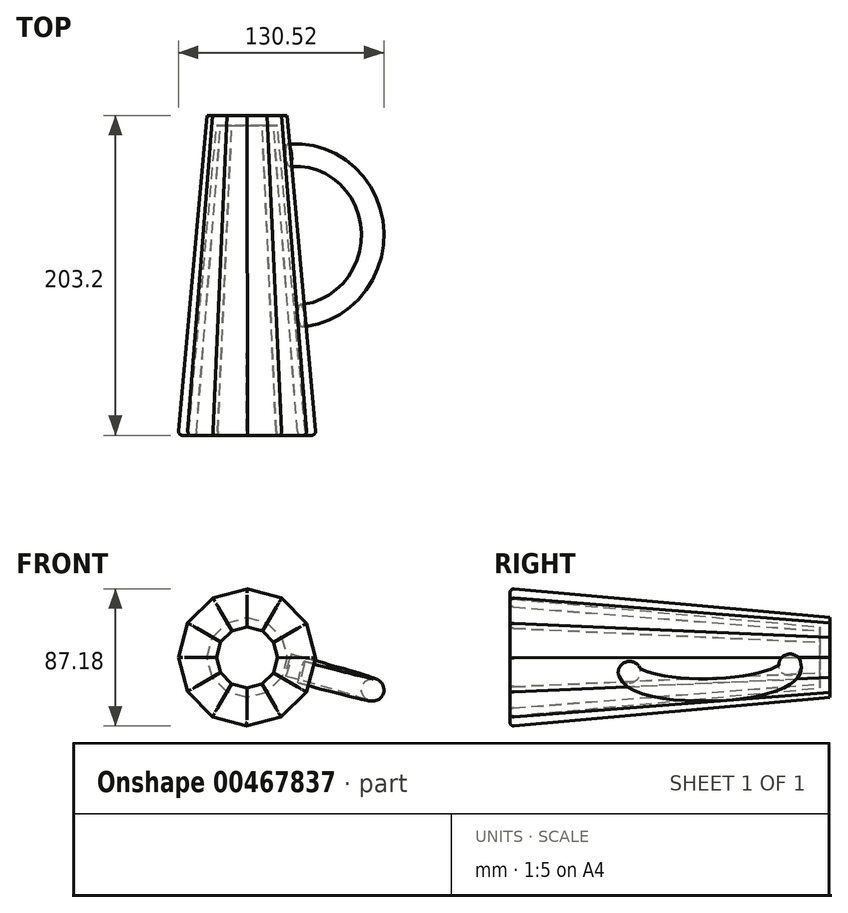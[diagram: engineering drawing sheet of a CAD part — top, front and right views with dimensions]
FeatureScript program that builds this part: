
annotation { "Feature Type Name" : "Feature", "Feature Type Description" : "" }
export const myFeature = defineFeature(function(context is Context, id is Id, definition is map)
    precondition{}
    {
        {
            var Q0;
            Q0=qCreatedBy(makeId("Front.planeOp"),FACE);
            var sketch = newSketch(context, id + "F0", { "sketchPlane" : qUnion([Q0])});
            skCircle(sketch, "E0.cCircle", {"center": v(0, 0) * mm, "radius": 24.56 * mm, "construction": true});
            skLineSegment(sketch, "E0.0", {"start": v(12.62, -22.07) * mm, "end": v(-0.1, -25.42) * mm});
            skLineSegment(sketch, "E0.1", {"start": v(-0.1, -25.42) * mm, "end": v(-12.8, -21.97) * mm});
            skLineSegment(sketch, "E0.2", {"start": v(-12.8, -21.97) * mm, "end": v(-22.07, -12.62) * mm});
            skLineSegment(sketch, "E0.3", {"start": v(-22.07, -12.62) * mm, "end": v(-25.42, 0.1) * mm});
            skLineSegment(sketch, "E0.4", {"start": v(-25.42, 0.1) * mm, "end": v(-21.97, 12.8) * mm});
            skLineSegment(sketch, "E0.5", {"start": v(-21.97, 12.8) * mm, "end": v(-12.62, 22.07) * mm});
            skLineSegment(sketch, "E0.6", {"start": v(-12.62, 22.07) * mm, "end": v(0.1, 25.42) * mm});
            skLineSegment(sketch, "E0.7", {"start": v(0.1, 25.42) * mm, "end": v(12.8, 21.97) * mm});
            skLineSegment(sketch, "E0.8", {"start": v(12.8, 21.97) * mm, "end": v(22.07, 12.62) * mm});
            skLineSegment(sketch, "E0.9", {"start": v(22.07, 12.62) * mm, "end": v(25.42, -0.1) * mm});
            skLineSegment(sketch, "E0.10", {"start": v(25.42, -0.1) * mm, "end": v(21.97, -12.8) * mm});
            skLineSegment(sketch, "E0.11", {"start": v(21.97, -12.8) * mm, "end": v(12.62, -22.07) * mm});
            skPoint(sketch, "E0.0.midPoint", {"position": v(6.26, -23.74) * mm});
            skSolve(sketch);
        }
        {
            var Q0;
            Q0=makeQuery(id+"F0.imprint","IMPRINT",FACE,{"disambiguationData":[TD([[makeQuery(id+"F0.imprint","IMPRINT",EDGE,{"derivedFrom":sQuery(id+"F0.wireOp",EDGE,"E0.0")}),-1.0]])]});
            extrude(context, id + "F1", {"entities" : qUnion([Q0]), "depth" : 203.2 * mm, "hasDraft" : true, "draftAngle" : 5 * degree});
        }
        {
            var Q0;
            Q0=makeQuery(id+"F1.opExtrude","CAP_FACE",FACE,{"disambiguationData":[OSD([sQuery(id+"F0.wireOp",EDGE,"E0.0"),sQuery(id+"F0.wireOp",EDGE,"E0.1"),sQuery(id+"F0.wireOp",EDGE,"E0.2"),sQuery(id+"F0.wireOp",EDGE,"E0.3"),sQuery(id+"F0.wireOp",EDGE,"E0.4"),sQuery(id+"F0.wireOp",EDGE,"E0.5"),sQuery(id+"F0.wireOp",EDGE,"E0.6"),sQuery(id+"F0.wireOp",EDGE,"E0.7"),sQuery(id+"F0.wireOp",EDGE,"E0.8"),sQuery(id+"F0.wireOp",EDGE,"E0.9"),sQuery(id+"F0.wireOp",EDGE,"E0.10"),sQuery(id+"F0.wireOp",EDGE,"E0.11")])],"isStart":false});
            shell(context, id + "F2", {"entities" : qUnion([Q0]), "thickness" : 6.35 * mm});
        }
        {
            var Q0;
            Q0=makeQuery(id+"F1.opExtrude","SWEPT_FACE",FACE,{"disambiguationData":[OSD([sQuery(id+"F0.wireOp",EDGE,"E0.10")])]});
            var sketch = newSketch(context, id + "F3", { "sketchPlane" : qUnion([Q0])});
            skCircle(sketch, "E1", {"center": v(-129.94, 0) * mm, "radius": 7.11 * mm});
            skLineSegment(sketch, "E2", {"start": v(-79.18, 19.24) * mm, "end": v(-78.24, -20.96) * mm});
            skSolve(sketch);
        }
        {
            var Q0;
            Q0 = qSketchRegion(id + "F3", true);
            var Q1;
            Q1=sQuery(id+"F3.wireOp",EDGE,"E2");
            revolve(context, id + "F4", {"operationType" : NewBodyOperationType.ADD, "entities" : qUnion([Q0]), "axis" : qUnion([Q1]), "revolveType" : RevolveType.ONE_DIRECTION, "oppositeDirection" : true, "angle" : 180 * degree});
        }
        {
            var Q0;
            Q0=makeQuery(id+"F1.opExtrude","CAP_FACE",FACE,{"disambiguationData":[OSD([sQuery(id+"F0.wireOp",EDGE,"E0.0"),sQuery(id+"F0.wireOp",EDGE,"E0.1"),sQuery(id+"F0.wireOp",EDGE,"E0.2"),sQuery(id+"F0.wireOp",EDGE,"E0.3"),sQuery(id+"F0.wireOp",EDGE,"E0.4"),sQuery(id+"F0.wireOp",EDGE,"E0.5"),sQuery(id+"F0.wireOp",EDGE,"E0.6"),sQuery(id+"F0.wireOp",EDGE,"E0.7"),sQuery(id+"F0.wireOp",EDGE,"E0.8"),sQuery(id+"F0.wireOp",EDGE,"E0.9"),sQuery(id+"F0.wireOp",EDGE,"E0.10"),sQuery(id+"F0.wireOp",EDGE,"E0.11")])],"isStart":false});
            fillet(context, id + "F5", {"entities" : qUnion([Q0]), "radius" : 2.54 * mm, "tangentPropagation" : true, "allowEdgeOverflow" : false});
        }
    });
